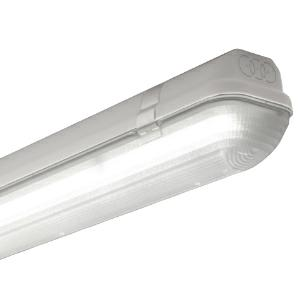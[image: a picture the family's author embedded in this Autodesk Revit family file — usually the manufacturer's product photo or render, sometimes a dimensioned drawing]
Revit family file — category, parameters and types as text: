
# Revit family: 3f_filippi_-_3f_linda_3f_filippi_-_58584_-_3f_linda_led_1x24w-865_l1270
name_source: partatom
category: Lighting Fixtures
units: mm (PartAtom-declared; Revit-internal decimal feet)

## family parameters
Cut with Voids When Loaded = No
Host = Face
Light Source = No
Part Type = Normal
Room Calculation Point = No
Round Connector Dimension = Use Diameter
Shared = No

## types (1)
- 3F Filippi - 3F Linda (1 x LED, 4065 lm, 28 W, 6500 K)
    Apparent Load = 28 VA
    Approval mark = CE
    CIE Flux Codes = 44 77 94 97 100
    Color Rendering = 80
    Color Temperature = 6500 K
    Control Gear = Electronic ballast
    Default Elevation = 1800 mm
    Description = ILLUMINOTECHNICAL
Luminous efficiency 100% (DLOR 97%, ULOR 3%).
Initial luminous flux of the luminaire 4065 lm.
Controlled symmetric distribution.
Installation Interdistance Transv.D = 1.77 x hu - Long.D = 1.17 x hu.
Tabular UGR (CIE 117 - 4H-8H; S=0.25H; 70/50/20): RUG 22 - 22.9.
Beam angle: 109° - 64°.
Luminous efficacy 145 lm/W.
Lifetime (L93/B10): 30000 h. (tq+25°C)
Lifetime (L90/B10): 50000 h. (tq+25°C)
Lifetime (L85/B10): 80000 h. (tq+25°C)
Lifetime (L80/B10): 100000 h. (tq+25°C)
Lifetime (L85/B10): 50000 h. (tq+35°C)
Sudden decreased luminous flux after 50000 hours: 0% (C0).
Photobiological safety in compliance with IEC/TR 62778: RG0 risk exempt, (IEC 62471).
In compliance with IEC/EN 62722-2-1 - IEC/EN 62717 standards.

SOURCE
Linear LED module 24W/865.
Energy efficiency class (UE 2019/2020 - UE 2019/2015): D.
CIE 13.3 Colour rendering index: CRI >80 (R9 <50%).
IES TM-30 Fidelity Index: Rf = 84 Rg = 95.
CCT nominal colour temperature 6500 K.
Colour initial tolerance (MacAdam): SDCM 3.

MECHANICAL
Self-extinguishing V2 polycarbonate housing, injection moulded, RAL 7035 grey.
Ecologic anti-aging injected sealing gasket.
Diffuser in self-extinguishing V2 polycarbonate, photo-engraved interior, UV stabilised, injection moulded with smooth outer surface, tamper-proof opening.
Gear-holder reflector in hot-dip galvanised steel, painted with white polyester base.
Snug fit safety snap-lock clips for diffuser mounting in stainless steel, screwdriver opening.
Fixing brackets in stainless steel.
Possibility for technicians to access the interior of the luminaire.
Luminaire with limited surface temperature. - D - (EN 60598-2-24)
Dimensions: 1270x100 mm, height 100 mm. Weight 2.049 kg.
IP66 protection degree.
Mechanical strength to impacts IK10 (20 joule).
Glow-wire test resistance 850°C.

ELECTRICAL
Halogen Free electronic wiring 230V-50/60Hz, power factor 0.90, THD <25%, constant output current, SELV, class I, 1 driver.
Power of the luminaire 28 W.
ENEC - CE.
SAFE FLICKER: PstLM=<1 and SVM=<0.4 (IEC TR 61547-1 and IEC TR 63158), to ensure a more comfortable and safe light.
Luminaire compliant with EN 60598-2-22 for power supply from a centralised emergency system CPSS (Central Power Supply System), not incorporated in the luminaire - high risk areas excluded. The default power and flux are 100% in AC and 100% in DC.
Ambient temperature from -20°C to +35°C.
Temperature class T6 max 85°C.
Relative humidity UR: <85%.

INSTALLATION
Ceiling / Suspended / Wall.
All accessories dedicated to this product are available on the Catalog and on our website www.3F-Filippi.com.

APPLICATIONS
Suitable product for food production plants (HACCP), IFS (Food Version 6), BRC (GSFS Food Version 7).
Dry, dusty indoor environments, subject to occasional water splashes.
Virtually shatterproof polycarbonate compatibly with the fumes / atmospheres that compromise the elasticity of plastic materials.
Not suitable for installation on surfaces subject to important vibrations, exposed to weather conditions, on ropes or poles.
Suitable for illumination of public car parks and parking grounds referred to DIN 67528:2018-04.

WARNING
Fixture not suitable for cold stores with an ambient temperature <0°C and/or relative humidity >85%.
Luminaire designed for disposal/recycling at end-of-life.
Replaceable (LED only) light source by a professional. Replaceable control gear by a professional.
    Height = 100 mm  [stored 0.328084 ft]
    Lamp = 1 x LED
    Lamp Light Flux = 4065 lm
    Lamp Power = 28 W
    Lamp count = 1
    Length = 1270 mm
    Lifetime = 50000 h
    Luminous efficacy = 145 lm/W
    Manufacturer = 3F Filippi
    ModVariant = No
    Model = 3F Filippi - 58584 - 3F Linda LED 1x24W-865 L1270
    Mounting Place = Ceiling
    Mounting Type = Pendant
    Number of Poles = 1
    OnlyDefault = Yes
    Power Factor = 1
    Product Name = 3F Filippi - 3F Linda
    Product group = pendant luminaire
    ProductGroupID = 9
    Protection Class = Protection class I
    Protection Degree = IP 66
    RLX_Detail_Level = 1
    RLX_Emergency_Light_Flux = 0 lm
    RLX_Emergency_Type = 0
    RLX_Emergency_Type_DB = No
    RlxData = <blob elided: 70677 chars, md5=78efaa7b>
    Socket = socket
    Standby Power = 0 W
    System Light Flux = 4065 lm
    System Power = 28 W
    Type Comments = Product without accessories
    Type Image = 3ffilippi_3f_linda_led.jpg
    URL = http://relux.com
    VarID = ---
    Voltage = 0 V
    Weight = 0.00 kg
    Width = 100 mm  [stored 0.328084 ft]

note: [stored X ft] marks values corroborated as IEEE doubles in the binary element streams (Revit-internal decimal feet)

## geometry (parser evidence)
native form markers: Blend x4, Sweep x7
no freeform markers — native parametric forms only
